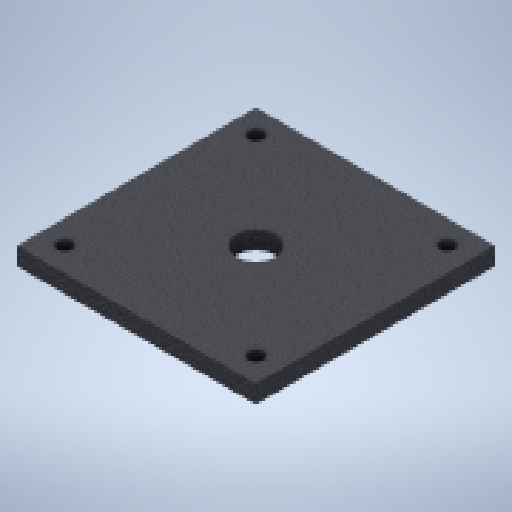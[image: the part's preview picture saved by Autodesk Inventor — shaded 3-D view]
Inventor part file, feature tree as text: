
AUTODESK INVENTOR PART (.ipt)
format: ipt  version: 2023 (Build 270158000, 158)  size: 178,176 bytes
history: native  units: mm
features: sketch x3, hole x2, other x1, extrude x1
ambient origin geometry x8: Origin, YZ Plane, XZ Plane, XY Plane, X Axis, Y Axis, Z Axis, Center Point
bodies: Body1 (feature_tree)
feature tree (7):
  other  "Sólido1"
  extrude  "Extrusão1"  Depth=80.0mm
  hole  "Furo1"  [1 undecoded]
  hole  "Furo2"  [1 undecoded]
  sketch  "Esboço1"  dims[d0=80.0mm d1=80.0mm]
  sketch  "Esboço2"  dims[d2=6.0mm d3=0.0mm d4=8.0mm]
  sketch  "Esboço3"  dims[d5=8.0mm d6=8.0mm d7=8.0mm d8=8.0mm d9=8.0mm d10=8.0mm d11=8.0mm d12=5.0mm d13=6.0mm d14=4.0mm d15=2.0mm d16=90.0deg d17=0.5mm d18=20.594885mm d19=80.0mm d20=40.0mm d21=40.0mm d22=13.0mm d23=6.0mm d24=4.0mm d25=2.0mm d26=90.0deg d27=8.0mm d28=20.594885mm]
note: 2 required parameter values undecoded (feature->parameter linkage not recoverable at this tier; creation-order binding heuristic only, values carry confidence <= 0.55)
